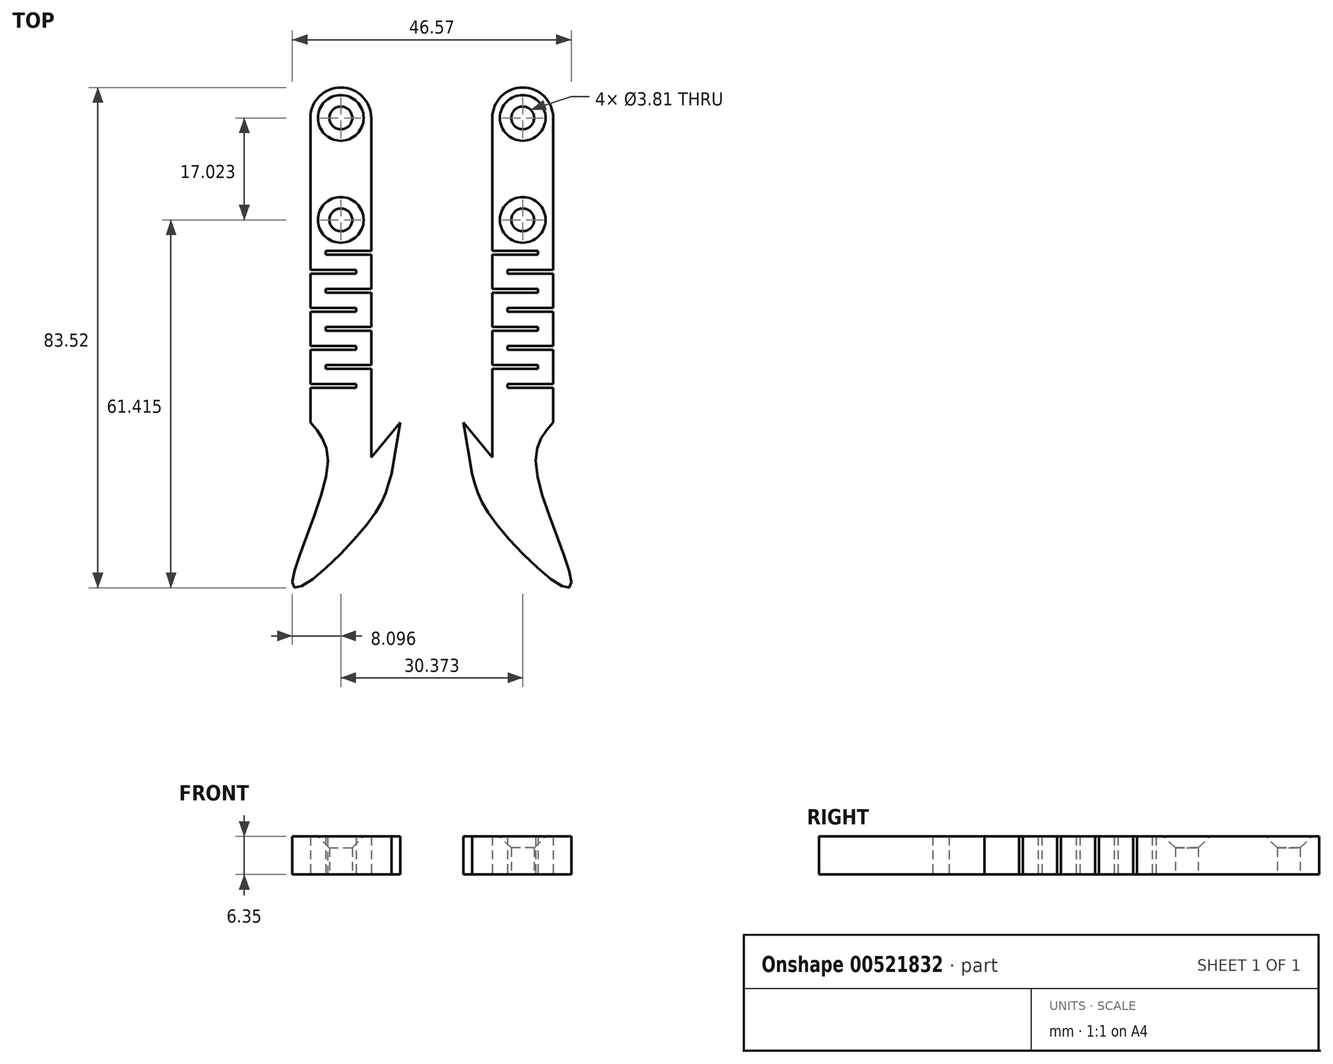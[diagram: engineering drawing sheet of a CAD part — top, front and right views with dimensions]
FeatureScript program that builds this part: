
annotation { "Feature Type Name" : "Feature", "Feature Type Description" : "" }
export const myFeature = defineFeature(function(context is Context, id is Id, definition is map)
    precondition{}
    {
        {
            var Q0;
            Q0=qCreatedBy(makeId("Top.planeOp"),FACE);
            var sketch = newSketch(context, id + "F0", { "sketchPlane" : qUnion([Q0])});
            skLineSegment(sketch, "E0", {"start": v(-2.54, -18.47) * mm, "end": v(-2.54, 19.63) * mm});
            skLineSegment(sketch, "E1", {"start": v(7.62, -18.47) * mm, "end": v(7.62, 32.33) * mm});
            skLineSegment(sketch, "E2.bottom", {"start": v(-2.54, 9.52) * mm, "end": v(5.08, 9.52) * mm});
            skLineSegment(sketch, "E2.top", {"start": v(-2.54, 10.16) * mm, "end": v(5.08, 10.16) * mm});
            skLineSegment(sketch, "E2.left", {"start": v(-2.54, 9.52) * mm, "end": v(-2.54, 10.16) * mm});
            skLineSegment(sketch, "E2.right", {"start": v(5.08, 9.52) * mm, "end": v(5.08, 10.16) * mm});
            skLineSegment(sketch, "E3", {"start": v(5.98, 6.99) * mm, "end": v(7.62, 6.99) * mm});
            skLineSegment(sketch, "E4.bottom", {"start": v(7.62, 6.99) * mm, "end": v(0, 6.99) * mm});
            skLineSegment(sketch, "E4.top", {"start": v(7.62, 6.35) * mm, "end": v(0, 6.35) * mm});
            skLineSegment(sketch, "E4.left", {"start": v(7.62, 6.99) * mm, "end": v(7.62, 6.35) * mm});
            skLineSegment(sketch, "E4.right", {"start": v(0, 6.99) * mm, "end": v(0, 6.35) * mm});
            skLineSegment(sketch, "E5", {"start": v(-2.54, 9.53) * mm, "end": v(-2.54, 3.81) * mm});
            skLineSegment(sketch, "E6", {"start": v(7.62, 6.35) * mm, "end": v(7.62, 0.63) * mm});
            skLineSegment(sketch, "E7.bottom", {"start": v(-2.54, 3.81) * mm, "end": v(5.08, 3.81) * mm});
            skLineSegment(sketch, "E7.top", {"start": v(-2.54, 3.18) * mm, "end": v(5.08, 3.18) * mm});
            skLineSegment(sketch, "E7.left", {"start": v(-2.54, 3.81) * mm, "end": v(-2.54, 3.17) * mm});
            skLineSegment(sketch, "E7.right", {"start": v(5.08, 3.81) * mm, "end": v(5.08, 3.18) * mm});
            skLineSegment(sketch, "E8.bottom", {"start": v(7.62, 0.63) * mm, "end": v(0, 0.63) * mm});
            skLineSegment(sketch, "E8.top", {"start": v(7.62, 0) * mm, "end": v(0, 0) * mm});
            skLineSegment(sketch, "E8.left", {"start": v(7.62, 0.63) * mm, "end": v(7.62, 0) * mm});
            skLineSegment(sketch, "E8.right", {"start": v(0, 0.63) * mm, "end": v(0, 0) * mm});
            skLineSegment(sketch, "E9", {"start": v(-2.54, 3.18) * mm, "end": v(-2.54, -2.54) * mm});
            skLineSegment(sketch, "E10", {"start": v(7.62, 0) * mm, "end": v(7.62, -5.71) * mm});
            skLineSegment(sketch, "E11.bottom", {"start": v(-2.54, -2.54) * mm, "end": v(5.08, -2.54) * mm});
            skLineSegment(sketch, "E11.top", {"start": v(-2.54, -3.17) * mm, "end": v(5.08, -3.17) * mm});
            skLineSegment(sketch, "E11.left", {"start": v(-2.54, -2.54) * mm, "end": v(-2.54, -3.17) * mm});
            skLineSegment(sketch, "E11.right", {"start": v(5.08, -2.54) * mm, "end": v(5.08, -3.17) * mm});
            skLineSegment(sketch, "E12.bottom", {"start": v(7.62, -5.71) * mm, "end": v(0, -5.71) * mm});
            skLineSegment(sketch, "E12.top", {"start": v(7.62, -6.35) * mm, "end": v(0, -6.35) * mm});
            skLineSegment(sketch, "E12.left", {"start": v(7.62, -5.71) * mm, "end": v(7.62, -6.35) * mm});
            skLineSegment(sketch, "E12.right", {"start": v(0, -5.72) * mm, "end": v(0, -6.35) * mm});
            skLineSegment(sketch, "E13", {"start": v(-2.54, -3.17) * mm, "end": v(-2.54, -8.89) * mm});
            skLineSegment(sketch, "E14", {"start": v(7.62, -6.35) * mm, "end": v(7.62, -12.07) * mm});
            skLineSegment(sketch, "E15.bottom", {"start": v(-2.54, -8.89) * mm, "end": v(5.08, -8.89) * mm});
            skLineSegment(sketch, "E15.top", {"start": v(-2.54, -9.53) * mm, "end": v(5.08, -9.53) * mm});
            skLineSegment(sketch, "E15.left", {"start": v(-2.54, -8.89) * mm, "end": v(-2.54, -9.53) * mm});
            skLineSegment(sketch, "E15.right", {"start": v(5.08, -8.89) * mm, "end": v(5.08, -9.53) * mm});
            skLineSegment(sketch, "E16.bottom", {"start": v(7.62, -12.07) * mm, "end": v(0, -12.07) * mm});
            skLineSegment(sketch, "E16.top", {"start": v(7.62, -12.7) * mm, "end": v(0, -12.7) * mm});
            skLineSegment(sketch, "E16.left", {"start": v(7.62, -12.06) * mm, "end": v(7.62, -12.7) * mm});
            skLineSegment(sketch, "E16.right", {"start": v(0, -12.07) * mm, "end": v(0, -12.7) * mm});
            skLineSegment(sketch, "E17", {"start": v(7.62, 9.52) * mm, "end": v(7.62, 6.99) * mm});
            skLineSegment(sketch, "E18", {"start": v(-2.54, 19.63) * mm, "end": v(-2.54, 32.33) * mm});
            skLineSegment(sketch, "E19", {"start": v(-2.54, 32.33) * mm, "end": v(7.62, 32.33) * mm});
            skCircle(sketch, "E20", {"center": v(2.54, 32.33) * mm, "radius": 5.08 * mm});
            skCircle(sketch, "E21", {"center": v(2.54, 32.33) * mm, "radius": 1.9 * mm});
            skCircle(sketch, "E22", {"center": v(2.54, 15.3) * mm, "radius": 1.9 * mm});
            skLineSegment(sketch, "E23", {"start": v(-7.37, -18.47) * mm, "end": v(-2.54, -24.37) * mm});
            skLineSegment(sketch, "E24", {"start": v(-2.54, -24.37) * mm, "end": v(-2.54, -18.47) * mm});
            skLineSegment(sketch, "E25", {"start": v(-7.37, -18.47) * mm, "end": v(-5.92, -27.12) * mm});
            skFitSpline(sketch, "E26", {"points": [v(-5.92, -27.12) * mm, v(-2.34, -34.87) * mm, v(10.4, -46) * mm, v(4.82, -26.5) * mm, v(7.62, -18.47) * mm], "startDerivative": vector(12.29, -39.9) * mm, "endDerivative": vector(25.4, 28.9) * mm});
            skSolve(sketch);
        }
        {
            var Q0;
            {var subQ1=sQuery(id+"F0.wireOp",EDGE,"E19");var subQ3=sQuery(id+"F0.wireOp",EDGE,"E21");var subQ4=makeQuery(id+"F0.imprint","INTERSECT",VERTEX,{"disambiguationData":[OD(0.0)],"derivedFrom":[subQ1,subQ3]});Q0=makeQuery(id+"F0.imprint","IMPRINT",FACE,{"disambiguationData":[TD([[makeQuery(id+"F0.imprint","IMPRINT",EDGE,{"disambiguationData":[TD([[subQ4,-1.0]])],"derivedFrom":subQ3}),-1.0]])]});}
            var Q1;
            {var subQ1=sQuery(id+"F0.wireOp",EDGE,"E19");var subQ3=sQuery(id+"F0.wireOp",EDGE,"E21");var subQ4=makeQuery(id+"F0.imprint","INTERSECT",VERTEX,{"disambiguationData":[OD(0.0)],"derivedFrom":[subQ1,subQ3]});Q1=makeQuery(id+"F0.imprint","IMPRINT",FACE,{"disambiguationData":[TD([[makeQuery(id+"F0.imprint","IMPRINT",EDGE,{"disambiguationData":[TD([[subQ4,1.0]])],"derivedFrom":subQ3}),-1.0]])]});}
            var Q2;
            Q2=makeQuery(id+"F0.imprint","IMPRINT",FACE,{"disambiguationData":[TD([[makeQuery(id+"F0.imprint","IMPRINT",EDGE,{"derivedFrom":sQuery(id+"F0.wireOp",EDGE,"E2.bottom")}),-1.0]])]});
            var Q3;
            {var subQ0=sQuery(id+"F0.wireOp",EDGE,"9e40b11a-283d-41bb-945c-c188b3fc0ce5");var subQ1=sQuery(id+"F0.wireOp",EDGE,"10f56092-dbf6-4593-aa57-fa7e99a8976d");var subQ2=makeQuery(id+"F0.imprint","INTERSECT",VERTEX,{"disambiguationData":[OD(0.0)],"derivedFrom":[subQ1,subQ0]});Q3=makeQuery(id+"F0.imprint","IMPRINT",FACE,{"disambiguationData":[TD([[makeQuery(id+"F0.imprint","IMPRINT",EDGE,{"disambiguationData":[TD([[subQ2,1.0]])],"derivedFrom":subQ1}),-1.0]])]});}
            extrude(context, id + "F1", {"entities" : qUnion([Q0, Q1, Q2, Q3]), "depth" : 6.35 * mm, "offsetDistance" : 25.4 * mm});
        }
        {
            var Q0;
            Q0=makeQuery(id+"F1.opExtrude","CAP_EDGE",EDGE,{"disambiguationData":[OSD([sQuery(id+"F0.wireOp",EDGE,"E22")])],"isStart":false});
            var Q1;
            Q1=makeQuery(id+"F1.opExtrude","CAP_EDGE",EDGE,{"disambiguationData":[OSD([sQuery(id+"F0.wireOp",EDGE,"E21")])],"isStart":false});
            chamfer(context, id + "F2", {"entities" : qUnion([Q0, Q1]), "width" : 1.9 * mm, "tangentPropagation" : true});
        }
        {
            var Q0;
            Q0=qCreatedBy(makeId("Top.planeOp"),FACE);
            var sketch = newSketch(context, id + "F3", { "sketchPlane" : qUnion([Q0])});
            skLineSegment(sketch, "E27", {"start": v(0, 0) * mm, "end": v(-34.07, 0) * mm});
            skLineSegment(sketch, "E28", {"start": v(-12.65, 0) * mm, "end": v(-12.65, 26.58) * mm});
            skSolve(sketch);
        }
        {
            var Q0;
            Q0=sQuery(id+"F3.wireOp",EDGE,"E28");
            extrude(context, id + "F4", {"bodyType" : ToolBodyType.SURFACE, "surfaceEntities" : qUnion([Q0]), "depth" : 25.4 * mm, "offsetDistance" : 25.4 * mm});
        }
        {
            var Q0;
            Q0=makeQuery(id+"F1.opExtrude","SWEPT_BODY",BODY,{"disambiguationData":[OSD([sQuery(id+"F0.wireOp",EDGE,"E0"),sQuery(id+"F0.wireOp",EDGE,"E1"),sQuery(id+"F0.wireOp",EDGE,"E2.bottom"),sQuery(id+"F0.wireOp",EDGE,"E2.top"),sQuery(id+"F0.wireOp",EDGE,"E2.right"),sQuery(id+"F0.wireOp",EDGE,"E4.bottom"),sQuery(id+"F0.wireOp",EDGE,"E4.top"),sQuery(id+"F0.wireOp",EDGE,"E4.right"),sQuery(id+"F0.wireOp",EDGE,"E5"),sQuery(id+"F0.wireOp",EDGE,"E7.bottom"),sQuery(id+"F0.wireOp",EDGE,"E7.top"),sQuery(id+"F0.wireOp",EDGE,"E7.right"),sQuery(id+"F0.wireOp",EDGE,"E8.bottom"),sQuery(id+"F0.wireOp",EDGE,"E8.top"),sQuery(id+"F0.wireOp",EDGE,"E8.right"),sQuery(id+"F0.wireOp",EDGE,"E9"),sQuery(id+"F0.wireOp",EDGE,"E10"),sQuery(id+"F0.wireOp",EDGE,"E11.bottom"),sQuery(id+"F0.wireOp",EDGE,"E11.top"),sQuery(id+"F0.wireOp",EDGE,"E11.right"),sQuery(id+"F0.wireOp",EDGE,"E12.bottom"),sQuery(id+"F0.wireOp",EDGE,"E12.top"),sQuery(id+"F0.wireOp",EDGE,"E12.right"),sQuery(id+"F0.wireOp",EDGE,"E13"),sQuery(id+"F0.wireOp",EDGE,"E14"),sQuery(id+"F0.wireOp",EDGE,"E15.bottom"),sQuery(id+"F0.wireOp",EDGE,"E15.top"),sQuery(id+"F0.wireOp",EDGE,"E15.right"),sQuery(id+"F0.wireOp",EDGE,"E16.bottom"),sQuery(id+"F0.wireOp",EDGE,"E16.top"),sQuery(id+"F0.wireOp",EDGE,"E16.right"),sQuery(id+"F0.wireOp",EDGE,"E6"),sQuery(id+"F0.wireOp",EDGE,"E17"),sQuery(id+"F0.wireOp",EDGE,"E18"),sQuery(id+"F0.wireOp",EDGE,"E20"),sQuery(id+"F0.wireOp",EDGE,"E21"),sQuery(id+"F0.wireOp",EDGE,"E22"),sQuery(id+"F0.wireOp",EDGE,"neLcBcqn-vR1B-IJLe-NEi5-yuCX7gkV3YYt"),sQuery(id+"F0.wireOp",EDGE,"BY62QiR2-CsrU-pXRa-kcyt-BKhnXDfwBt9G"),sQuery(id+"F0.wireOp",EDGE,"10f56092-dbf6-4593-aa57-fa7e99a8976d"),sQuery(id+"F0.wireOp",EDGE,"9e40b11a-283d-41bb-945c-c188b3fc0ce5")])]});
            var Q1;
            Q1=makeQuery(id+"F4.opExtrude","SWEPT_FACE",FACE,{"disambiguationData":[OSD([sQuery(id+"F3.wireOp",EDGE,"E28")])]});
            mirror(context, id + "F5", {"entities" : qUnion([Q0]), "mirrorPlane" : qUnion([Q1])});
        }
    });
